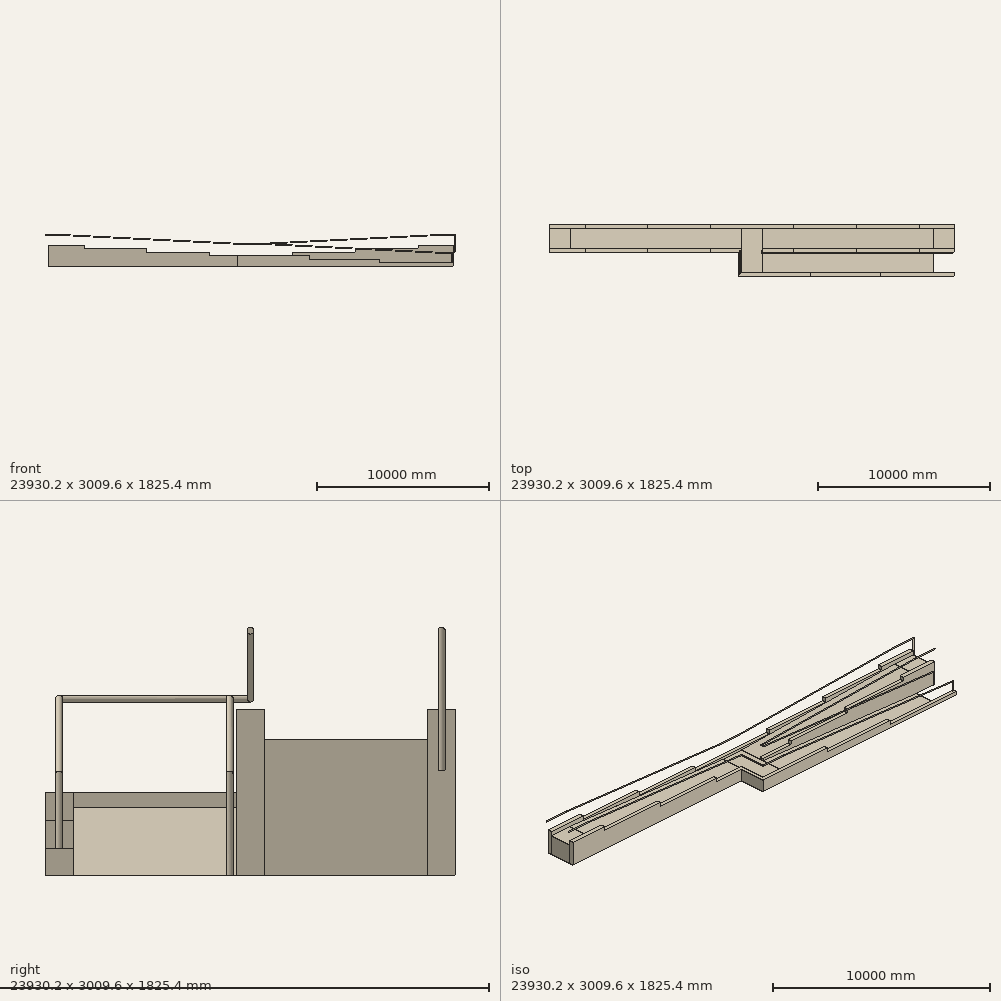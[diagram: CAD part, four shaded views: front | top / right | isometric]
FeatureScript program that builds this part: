
annotation { "Feature Type Name" : "Feature", "Feature Type Description" : "" }
export const myFeature = defineFeature(function(context is Context, id is Id, definition is map)
    precondition{}
    {
        {
            var Q0;
            Q0=qCreatedBy(makeId("Front.planeOp"),FACE);
            var sketch = newSketch(context, id + "F0", { "sketchPlane" : qUnion([Q0])});
            skLineSegment(sketch, "E0", {"start": v(0, 0) * mm, "end": v(-11200, 0) * mm});
            skLineSegment(sketch, "E1", {"start": v(-11200, 0) * mm, "end": v(-11200, 500) * mm});
            skLineSegment(sketch, "E2", {"start": v(-11200, 500) * mm, "end": v(-10000, 500) * mm});
            skLineSegment(sketch, "E3", {"start": v(-10000, 500) * mm, "end": v(0, 0) * mm});
            skLineSegment(sketch, "E4", {"start": v(0, 0) * mm, "end": v(1200, 0) * mm});
            skLineSegment(sketch, "E5", {"start": v(1200, 0) * mm, "end": v(1200, 1000) * mm});
            skLineSegment(sketch, "E6", {"start": v(1200, 1000) * mm, "end": v(0, 1000) * mm});
            skLineSegment(sketch, "E7", {"start": v(0, 1000) * mm, "end": v(-10000, 500) * mm});
            skLineSegment(sketch, "E8", {"start": v(0, 1000) * mm, "end": v(0, 0) * mm, "construction": true});
            skLineSegment(sketch, "E9", {"start": v(-10600, 500) * mm, "end": v(-10600, 2597.13) * mm, "construction": true});
            skLineSegment(sketch, "E10.MirrorCS", {"start": v(-21200, 1000) * mm, "end": v(-11200, 500) * mm});
            skLineSegment(sketch, "E11.MirrorCS", {"start": v(-22400, 1000) * mm, "end": v(-21200, 1000) * mm});
            skLineSegment(sketch, "E12.MirrorCS", {"start": v(-22400, 0) * mm, "end": v(-22400, 1000) * mm});
            skLineSegment(sketch, "E13.MirrorCS", {"start": v(-21200, 0) * mm, "end": v(-22400, 0) * mm});
            skLineSegment(sketch, "E14.MirrorCS", {"start": v(-21200, 0) * mm, "end": v(-10000, 0) * mm});
            skSolve(sketch);
        }
        {
            var Q0;
            Q0=makeQuery(id+"F0.imprint","IMPRINT",FACE,{"disambiguationData":[TD([[makeQuery(id+"F0.imprint","IMPRINT",EDGE,{"derivedFrom":sQuery(id+"F0.wireOp",EDGE,"E0")}),-1.0]])]});
            extrude(context, id + "F1", {"entities" : qUnion([Q0]), "depth" : 1200 * mm, "offsetDistance" : 25 * mm});
        }
        {
            var Q0;
            Q0=makeQuery(id+"F0.imprint","IMPRINT",FACE,{"disambiguationData":[TD([[makeQuery(id+"F0.imprint","IMPRINT",EDGE,{"derivedFrom":sQuery(id+"F0.wireOp",EDGE,"E3")}),1.0]])]});
            var Q1;
            Q1=makeQuery(id+"F0.imprint","IMPRINT",FACE,{"disambiguationData":[TD([[makeQuery(id+"F0.imprint","IMPRINT",EDGE,{"derivedFrom":sQuery(id+"F0.wireOp",EDGE,"E0")}),-1.0]])]});
            var Q2;
            {var subQ0=sQuery(id+"F0.wireOp",EDGE,"E1");Q2=makeQuery(id+"F0.imprint","IMPRINT",FACE,{"disambiguationData":[TD([[makeQuery(id+"F0.imprint","IMPRINT",EDGE,{"derivedFrom":subQ0}),1.0]])]});}
            extrude(context, id + "F2", {"entities" : qUnion([Q0, Q1, Q2]), "operationType" : NewBodyOperationType.ADD, "oppositeDirection" : true, "depth" : 203.2 * mm + 1200 * mm, "offsetDistance" : 25 * mm});
        }
        {
            var Q0;
            Q0=qCreatedBy(makeId("Top.planeOp"),FACE);
            var sketch = newSketch(context, id + "F3", { "sketchPlane" : qUnion([Q0])});
            skLineSegment(sketch, "E15.0", {"start": v(1200, 0) * mm, "end": v(0, 0) * mm, "construction": true});
            skLineSegment(sketch, "E15.1", {"start": v(-11200, 0) * mm, "end": v(-10000, 0) * mm, "construction": true});
            skLineSegment(sketch, "E16.bottom", {"start": v(-11200, 0) * mm, "end": v(1200, 0) * mm});
            skLineSegment(sketch, "E16.top", {"start": v(-10000, 203.2) * mm, "end": v(1200, 203.2) * mm});
            skLineSegment(sketch, "E16.left", {"start": v(-10000, 0) * mm, "end": v(-10000, 203.2) * mm});
            skLineSegment(sketch, "E16.right", {"start": v(1200, 0) * mm, "end": v(1200, 203.2) * mm});
            skLineSegment(sketch, "E17", {"start": v(-10600, 0) * mm, "end": v(-10600, 1718.88) * mm, "construction": true});
            skLineSegment(sketch, "E18.MirrorCS", {"start": v(-22400, 0) * mm, "end": v(-22400, 203.2) * mm});
            skLineSegment(sketch, "E19.MirrorCS", {"start": v(-11200, 0) * mm, "end": v(-11200, 203.2) * mm});
            skLineSegment(sketch, "E20.MirrorCS", {"start": v(-10000, 0) * mm, "end": v(-11200, 0) * mm, "construction": true});
            skLineSegment(sketch, "E21.MirrorCS", {"start": v(-22400, 0) * mm, "end": v(-21200, 0) * mm, "construction": true});
            skLineSegment(sketch, "E22.MirrorCS", {"start": v(-10000, 0) * mm, "end": v(-22400, 0) * mm});
            skLineSegment(sketch, "E23.MirrorCS", {"start": v(-11200, 203.2) * mm, "end": v(-22400, 203.2) * mm});
            skSolve(sketch);
        }
        {
            var Q0;
            Q0 = qSketchRegion(id + "F3", true);
            extrude(context, id + "F4", {"entities" : qUnion([Q0]), "operationType" : NewBodyOperationType.REMOVE, "endBound" : BoundingType.THROUGH_ALL, "depth" : 25 * mm, "offsetDistance" : 25 * mm});
        }
        {
            var Q0;
            Q0=sQuery(id+"F0.wireOp",EDGE,"E4");
            extrude(context, id + "F5", {"bodyType" : ToolBodyType.SURFACE, "surfaceEntities" : qUnion([Q0]), "depth" : 1200 * mm, "offsetDistance" : 25 * mm});
        }
        {
            var Q0;
            Q0=makeQuery(id+"F4.boolean.opBoolean","COPY",FACE,{"derivedFrom":makeQuery(id+"F4.opExtrude","SWEPT_FACE",FACE,{"disambiguationData":[OSD([sQuery(id+"F3.wireOp",EDGE,"E16.top")])]})});
            var sketch = newSketch(context, id + "F6", { "sketchPlane" : qUnion([Q0])});
            skLineSegment(sketch, "E24", {"start": v(-10000, 0) * mm, "end": v(-10000, 609.6) * mm});
            skLineSegment(sketch, "E25", {"start": v(-10000, 609.6) * mm, "end": v(-8171.2, 609.6) * mm});
            skLineSegment(sketch, "E26", {"start": v(-8171.2, 609.6) * mm, "end": v(-8171.2, 812.8) * mm});
            skLineSegment(sketch, "E27.1.0.1", {"start": v(-8171.2, 812.8) * mm, "end": v(-4513.6, 812.8) * mm});
            skLineSegment(sketch, "E28.1.0.0", {"start": v(-4513.6, 812.8) * mm, "end": v(-4513.6, 1016) * mm});
            skLineSegment(sketch, "E28.1.0.1", {"start": v(-4513.6, 1016) * mm, "end": v(-856, 1016) * mm});
            skLineSegment(sketch, "E28.2.0.0", {"start": v(-856, 1016) * mm, "end": v(-856, 1219.2) * mm});
            skLineSegment(sketch, "E28.direction1", {"start": v(-8171.2, 609.6) * mm, "end": v(-4513.6, 812.8) * mm, "construction": true});
            skLineSegment(sketch, "E29", {"start": v(-856, 1219.2) * mm, "end": v(1200, 1219.2) * mm});
            skLineSegment(sketch, "E30", {"start": v(1200, 1219.2) * mm, "end": v(1200, 0) * mm});
            skLineSegment(sketch, "E31", {"start": v(1200, 0) * mm, "end": v(-10000, 0) * mm});
            skLineSegment(sketch, "E32", {"start": v(-10600.94, 500.76) * mm, "end": v(-10600.94, 1723.23) * mm, "construction": true});
            skLineSegment(sketch, "E33.MirrorCS", {"start": v(-20345.88, 1016) * mm, "end": v(-20345.88, 1219.2) * mm});
            skLineSegment(sketch, "E34.MirrorCS", {"start": v(-13030.68, 609.6) * mm, "end": v(-13030.68, 812.8) * mm});
            skLineSegment(sketch, "E35.MirrorCS", {"start": v(-16688.28, 812.8) * mm, "end": v(-16688.28, 1016) * mm});
            skLineSegment(sketch, "E36.MirrorCS", {"start": v(-22401.88, 0) * mm, "end": v(-11201.88, 0) * mm});
            skLineSegment(sketch, "E37.MirrorCS", {"start": v(-20345.88, 1219.2) * mm, "end": v(-22401.88, 1219.2) * mm});
            skLineSegment(sketch, "E38.MirrorCS", {"start": v(-13030.68, 812.8) * mm, "end": v(-16688.28, 812.8) * mm});
            skLineSegment(sketch, "E39.MirrorCS", {"start": v(-11201.88, 0) * mm, "end": v(-11201.88, 609.6) * mm});
            skLineSegment(sketch, "E40.MirrorCS", {"start": v(-11201.88, 609.6) * mm, "end": v(-13030.68, 609.6) * mm});
            skLineSegment(sketch, "E41.MirrorCS", {"start": v(-13030.68, 609.6) * mm, "end": v(-16688.28, 812.8) * mm, "construction": true});
            skLineSegment(sketch, "E42.MirrorCS", {"start": v(-22401.88, 1219.2) * mm, "end": v(-22401.88, 0) * mm});
            skLineSegment(sketch, "E43.MirrorCS", {"start": v(-16688.28, 1016) * mm, "end": v(-20345.88, 1016) * mm});
            skSolve(sketch);
        }
        {
            var Q0;
            Q0 = qSketchRegion(id + "F6", true);
            extrude(context, id + "F7", {"entities" : qUnion([Q0]), "depth" : 203.2 * mm, "offsetDistance" : 25 * mm});
        }
        {
            var Q0;
            Q0=makeQuery(id+"F2.opExtrude","CAP_FACE",FACE,{"disambiguationData":[OSD([sQuery(id+"F0.wireOp",EDGE,"E0"),sQuery(id+"F0.wireOp",EDGE,"E1"),sQuery(id+"F0.wireOp",EDGE,"E2"),sQuery(id+"F0.wireOp",EDGE,"E4"),sQuery(id+"F0.wireOp",EDGE,"E5"),sQuery(id+"F0.wireOp",EDGE,"E6"),sQuery(id+"F0.wireOp",EDGE,"E7")])],"isStart":false});
            var sketch = newSketch(context, id + "F8", { "sketchPlane" : qUnion([Q0])});
            skLineSegment(sketch, "E44.0.0", {"start": v(10000, 0) * mm, "end": v(10000, 609.6) * mm, "construction": true});
            skLineSegment(sketch, "E44.0.1", {"start": v(10000, 609.6) * mm, "end": v(8171.2, 609.6) * mm});
            skLineSegment(sketch, "E44.0.2", {"start": v(8171.2, 609.6) * mm, "end": v(8171.2, 812.8) * mm});
            skLineSegment(sketch, "E44.0.3", {"start": v(8171.2, 812.8) * mm, "end": v(4513.6, 812.8) * mm});
            skLineSegment(sketch, "E44.0.4", {"start": v(4513.6, 812.8) * mm, "end": v(4513.6, 1016) * mm});
            skLineSegment(sketch, "E44.0.5", {"start": v(4513.6, 1016) * mm, "end": v(856, 1016) * mm});
            skLineSegment(sketch, "E44.0.6", {"start": v(856, 1016) * mm, "end": v(856, 1219.2) * mm});
            skLineSegment(sketch, "E44.0.7", {"start": v(856, 1219.2) * mm, "end": v(-1200, 1219.2) * mm});
            skLineSegment(sketch, "E44.0.8", {"start": v(-1200, 1219.2) * mm, "end": v(-1200, 0) * mm});
            skLineSegment(sketch, "E44.0.9", {"start": v(-1200, 0) * mm, "end": v(10000, 0) * mm});
            skLineSegment(sketch, "E45", {"start": v(11200, 609.6) * mm, "end": v(10000, 609.6) * mm});
            skLineSegment(sketch, "E46", {"start": v(10600, 609.6) * mm, "end": v(10600, -570.65) * mm, "construction": true});
            skLineSegment(sketch, "E47.MirrorCS", {"start": v(11200, 609.6) * mm, "end": v(13028.8, 609.6) * mm});
            skLineSegment(sketch, "E48.MirrorCS", {"start": v(13028.8, 609.6) * mm, "end": v(13028.8, 812.8) * mm});
            skLineSegment(sketch, "E49.MirrorCS", {"start": v(20344, 1016) * mm, "end": v(20344, 1219.2) * mm});
            skLineSegment(sketch, "E50.MirrorCS", {"start": v(16686.4, 812.8) * mm, "end": v(16686.4, 1016) * mm});
            skLineSegment(sketch, "E51.MirrorCS", {"start": v(16686.4, 1016) * mm, "end": v(20344, 1016) * mm});
            skLineSegment(sketch, "E52.MirrorCS", {"start": v(13028.8, 812.8) * mm, "end": v(16686.4, 812.8) * mm});
            skLineSegment(sketch, "E53.MirrorCS", {"start": v(22400, 1219.2) * mm, "end": v(22400, 0) * mm});
            skLineSegment(sketch, "E54.MirrorCS", {"start": v(20344, 1219.2) * mm, "end": v(22400, 1219.2) * mm});
            skLineSegment(sketch, "E55.MirrorCS", {"start": v(22400, 0) * mm, "end": v(11200, 0) * mm});
            skLineSegment(sketch, "E56", {"start": v(11200, 0) * mm, "end": v(10000, 0) * mm});
            skSolve(sketch);
        }
        {
            var Q0;
            Q0 = qSketchRegion(id + "F8", true);
            extrude(context, id + "F9", {"entities" : qUnion([Q0]), "depth" : 203.2 * mm, "offsetDistance" : 25 * mm});
        }
        {
            var Q0;
            Q0=makeQuery(id+"F1.opExtrude","SWEPT_FACE",FACE,{"disambiguationData":[OSD([sQuery(id+"F0.wireOp",EDGE,"E1")])]});
            var sketch = newSketch(context, id + "F10", { "sketchPlane" : qUnion([Q0])});
            skLineSegment(sketch, "E57.top", {"start": v(0, 0) * mm, "end": v(1200, 0) * mm});
            skLineSegment(sketch, "E57.right", {"start": v(1200, 609.6) * mm, "end": v(1200, 0) * mm, "construction": true});
            skLineSegment(sketch, "E58", {"start": v(1200, 609.6) * mm, "end": v(1403.2, 609.6) * mm});
            skLineSegment(sketch, "E59", {"start": v(1403.2, 609.6) * mm, "end": v(1403.2, 0) * mm});
            skLineSegment(sketch, "E60", {"start": v(1403.2, 0) * mm, "end": v(1200, 0) * mm});
            skLineSegment(sketch, "E61", {"start": v(1200, 609.6) * mm, "end": v(0, 609.6) * mm});
            skLineSegment(sketch, "E62", {"start": v(0, 609.6) * mm, "end": v(0, 0) * mm});
            skSolve(sketch);
        }
        {
            var Q0;
            Q0 = qSketchRegion(id + "F10", true);
            extrude(context, id + "F11", {"entities" : qUnion([Q0]), "operationType" : NewBodyOperationType.ADD, "depth" : 203.2 * mm, "offsetDistance" : 25 * mm});
        }
        {
            var Q0;
            Q0=makeQuery(id+"F1.opExtrude","CAP_FACE",FACE,{"disambiguationData":[OSD([sQuery(id+"F0.wireOp",EDGE,"E0"),sQuery(id+"F0.wireOp",EDGE,"E1"),sQuery(id+"F0.wireOp",EDGE,"E2"),sQuery(id+"F0.wireOp",EDGE,"E3")])],"isStart":false});
            var sketch = newSketch(context, id + "F12", { "sketchPlane" : qUnion([Q0])});
            skLineSegment(sketch, "E63", {"start": v(-11200, 500) * mm, "end": v(-11200, 609.6) * mm});
            skLineSegment(sketch, "E64", {"start": v(-11200, 609.6) * mm, "end": v(-7200, 609.6) * mm});
            skLineSegment(sketch, "E65", {"start": v(-7200, 609.6) * mm, "end": v(-7200, 406.4) * mm});
            skLineSegment(sketch, "E66", {"start": v(-7200, 406.4) * mm, "end": v(-3136, 406.4) * mm});
            skLineSegment(sketch, "E67.1.0.0", {"start": v(-3136, 406.4) * mm, "end": v(-3136, 203.2) * mm});
            skLineSegment(sketch, "E67.1.0.1", {"start": v(-3136, 203.2) * mm, "end": v(928, 203.2) * mm});
            skLineSegment(sketch, "E67.direction1", {"start": v(-7200, 406.4) * mm, "end": v(-3136, 203.2) * mm, "construction": true});
            skLineSegment(sketch, "E68.0", {"start": v(1200, 0) * mm, "end": v(1200, 1000) * mm, "construction": true});
            skLineSegment(sketch, "E69", {"start": v(928, 203.2) * mm, "end": v(1200, 203.2) * mm});
            skLineSegment(sketch, "E70", {"start": v(1200, 203.2) * mm, "end": v(1200, 0) * mm});
            skLineSegment(sketch, "E71", {"start": v(-11200, 500) * mm, "end": v(-11200, 0) * mm});
            skLineSegment(sketch, "E72", {"start": v(-11200, 0) * mm, "end": v(1200, 0) * mm});
            skSolve(sketch);
        }
        {
            var Q0;
            Q0 = qSketchRegion(id + "F12", true);
            extrude(context, id + "F13", {"entities" : qUnion([Q0]), "operationType" : NewBodyOperationType.ADD, "depth" : 203.2 * mm, "offsetDistance" : 25 * mm});
        }
        {
            var Q0;
            Q0=makeQuery(id+"F13.opExtrude","CAP_FACE",FACE,{"disambiguationData":[OSD([sQuery(id+"F12.wireOp",EDGE,"E63"),sQuery(id+"F12.wireOp",EDGE,"E64"),sQuery(id+"F12.wireOp",EDGE,"E65"),sQuery(id+"F12.wireOp",EDGE,"E66"),sQuery(id+"F12.wireOp",EDGE,"E67.1.0.0"),sQuery(id+"F12.wireOp",EDGE,"E67.1.0.1"),sQuery(id+"F12.wireOp",EDGE,"E69"),sQuery(id+"F12.wireOp",EDGE,"E70"),sQuery(id+"F12.wireOp",EDGE,"E71"),sQuery(id+"F12.wireOp",EDGE,"E72")])],"isStart":false});
            var Q1;
            Q1=makeQuery(id+"F13.opExtrude","CAP_FACE",FACE,{"disambiguationData":[OSD([sQuery(id+"F12.wireOp",EDGE,"E63"),sQuery(id+"F12.wireOp",EDGE,"E64"),sQuery(id+"F12.wireOp",EDGE,"E65"),sQuery(id+"F12.wireOp",EDGE,"E66"),sQuery(id+"F12.wireOp",EDGE,"E67.1.0.0"),sQuery(id+"F12.wireOp",EDGE,"E67.1.0.1"),sQuery(id+"F12.wireOp",EDGE,"E69"),sQuery(id+"F12.wireOp",EDGE,"E70"),sQuery(id+"F12.wireOp",EDGE,"E71"),sQuery(id+"F12.wireOp",EDGE,"E72")])],"isStart":true});
            cPlane(context, id + "F14", {"entities" : qUnion([Q0, Q1]), "cplaneType" : CPlaneType.MID_PLANE, "offset" : 25 * mm, "width" : 150 * mm, "height" : 150 * mm});
        }
        {
            var Q0;
            Q0=qCreatedBy(id+"F14.planeOp",FACE);
            var sketch = newSketch(context, id + "F15", { "sketchPlane" : qUnion([Q0])});
            skLineSegment(sketch, "E73", {"start": v(1098.4, 0) * mm, "end": v(1098.4, 745.08) * mm});
            skLineSegment(sketch, "E74", {"start": v(1098.4, 745.08) * mm, "end": v(-10000, 1300) * mm});
            skLineSegment(sketch, "E75", {"start": v(-10000, 1300) * mm, "end": v(-10000, 609.6) * mm, "construction": true});
            skLineSegment(sketch, "E76", {"start": v(0, 0) * mm, "end": v(0, 800) * mm, "construction": true});
            skSolve(sketch);
        }
        {
            var Q0;
            {var subQ0=sQuery(id+"F0.wireOp",EDGE,"E2");Q0=makeQuery(id+"F2.boolean.opBoolean","MERGE",FACE,{"derivedFrom":[makeQuery(id+"F1.opExtrude","SWEPT_FACE",FACE,{"disambiguationData":[OSD([subQ0])]}),makeQuery(id+"F2.opExtrude","SWEPT_FACE",FACE,{"disambiguationData":[OSD([subQ0])]})]});}
            var Q1;
            Q1=sQuery(id+"F15.wireOp",VERTEX,"E75.start");
            cPlane(context, id + "F16", {"entities" : qUnion([Q0, Q1]), "cplaneType" : CPlaneType.PLANE_POINT, "offset" : 25 * mm, "width" : 150 * mm, "height" : 150 * mm});
        }
        {
            var Q0;
            Q0=makeQuery(id+"F9.opExtrude","CAP_FACE",FACE,{"disambiguationData":[OSD([sQuery(id+"F8.wireOp",EDGE,"E44.0.1"),sQuery(id+"F8.wireOp",EDGE,"E44.0.2"),sQuery(id+"F8.wireOp",EDGE,"E44.0.3"),sQuery(id+"F8.wireOp",EDGE,"E44.0.4"),sQuery(id+"F8.wireOp",EDGE,"E44.0.5"),sQuery(id+"F8.wireOp",EDGE,"E44.0.6"),sQuery(id+"F8.wireOp",EDGE,"E44.0.7"),sQuery(id+"F8.wireOp",EDGE,"E44.0.8"),sQuery(id+"F8.wireOp",EDGE,"E44.0.9"),sQuery(id+"F8.wireOp",EDGE,"E45"),sQuery(id+"F8.wireOp",EDGE,"E48.MirrorCS"),sQuery(id+"F8.wireOp",EDGE,"E49.MirrorCS"),sQuery(id+"F8.wireOp",EDGE,"E50.MirrorCS"),sQuery(id+"F8.wireOp",EDGE,"E51.MirrorCS"),sQuery(id+"F8.wireOp",EDGE,"E52.MirrorCS"),sQuery(id+"F8.wireOp",EDGE,"E53.MirrorCS"),sQuery(id+"F8.wireOp",EDGE,"E47.MirrorCS"),sQuery(id+"F8.wireOp",EDGE,"E54.MirrorCS"),sQuery(id+"F8.wireOp",EDGE,"E55.MirrorCS"),sQuery(id+"F8.wireOp",EDGE,"E56")])],"isStart":true});
            var Q1;
            Q1=makeQuery(id+"F9.opExtrude","CAP_FACE",FACE,{"disambiguationData":[OSD([sQuery(id+"F8.wireOp",EDGE,"E44.0.1"),sQuery(id+"F8.wireOp",EDGE,"E44.0.2"),sQuery(id+"F8.wireOp",EDGE,"E44.0.3"),sQuery(id+"F8.wireOp",EDGE,"E44.0.4"),sQuery(id+"F8.wireOp",EDGE,"E44.0.5"),sQuery(id+"F8.wireOp",EDGE,"E44.0.6"),sQuery(id+"F8.wireOp",EDGE,"E44.0.7"),sQuery(id+"F8.wireOp",EDGE,"E44.0.8"),sQuery(id+"F8.wireOp",EDGE,"E44.0.9"),sQuery(id+"F8.wireOp",EDGE,"E45"),sQuery(id+"F8.wireOp",EDGE,"E48.MirrorCS"),sQuery(id+"F8.wireOp",EDGE,"E49.MirrorCS"),sQuery(id+"F8.wireOp",EDGE,"E50.MirrorCS"),sQuery(id+"F8.wireOp",EDGE,"E51.MirrorCS"),sQuery(id+"F8.wireOp",EDGE,"E52.MirrorCS"),sQuery(id+"F8.wireOp",EDGE,"E53.MirrorCS"),sQuery(id+"F8.wireOp",EDGE,"E47.MirrorCS"),sQuery(id+"F8.wireOp",EDGE,"E54.MirrorCS"),sQuery(id+"F8.wireOp",EDGE,"E55.MirrorCS"),sQuery(id+"F8.wireOp",EDGE,"E56")])],"isStart":false});
            cPlane(context, id + "F17", {"entities" : qUnion([Q0, Q1]), "cplaneType" : CPlaneType.MID_PLANE, "offset" : 25 * mm, "width" : 150 * mm, "height" : 150 * mm});
        }
        {
            var Q0;
            Q0=qCreatedBy(id+"F16.planeOp",FACE);
            var sketch = newSketch(context, id + "F18", { "sketchPlane" : qUnion([Q0])});
            skLineSegment(sketch, "E77", {"start": v(-10000, -1301.6) * mm, "end": v(-11301.6, -1301.6) * mm});
            skLineSegment(sketch, "E78.0", {"start": v(-11200, 1403.2) * mm, "end": v(-11200, -1200) * mm, "construction": true});
            skLineSegment(sketch, "E78.1", {"start": v(-11403.2, 1606.4) * mm, "end": v(-11403.2, -1403.2) * mm, "construction": true});
            skLineSegment(sketch, "E79", {"start": v(-11200, -1200) * mm, "end": v(-11403.2, -1403.2) * mm, "construction": true});
            skLineSegment(sketch, "E80", {"start": v(-11403.2, 1606.4) * mm, "end": v(-11200, 1403.2) * mm, "construction": true});
            skLineSegment(sketch, "E81", {"start": v(-11301.6, -1301.6) * mm, "end": v(-11301.6, 101.6) * mm});
            skLineSegment(sketch, "E82", {"start": v(-11301.6, 1504.8) * mm, "end": v(-10000, 1504.8) * mm});
            skLineSegment(sketch, "E83", {"start": v(-10000, -1301.6) * mm, "end": v(-10000, 1504.8) * mm, "construction": true});
            skLineSegment(sketch, "E84.0", {"start": v(-10000, 0) * mm, "end": v(-10000, 203.2) * mm, "construction": true});
            skLineSegment(sketch, "E85", {"start": v(-10000, 101.6) * mm, "end": v(-10000, -50.8) * mm});
            skPoint(sketch, "E86", {"position": v(-11301.6, 101.6) * mm});
            skSolve(sketch);
        }
        {
            var Q0;
            Q0=qCreatedBy(id+"F17.planeOp",FACE);
            var sketch = newSketch(context, id + "F19", { "sketchPlane" : qUnion([Q0])});
            skLineSegment(sketch, "E87", {"start": v(0, 1800) * mm, "end": v(-10000, 1300) * mm});
            skLineSegment(sketch, "E88", {"start": v(1301.6, 1800) * mm, "end": v(0, 1800) * mm});
            skLineSegment(sketch, "E89", {"start": v(1301.6, 1800) * mm, "end": v(1301.6, 773.02) * mm});
            skPoint(sketch, "E90", {"position": v(-10650.8, 1300) * mm});
            skLineSegment(sketch, "E91", {"start": v(-10650.8, 1300) * mm, "end": v(-10650.8, 959.1) * mm, "construction": true});
            skLineSegment(sketch, "E92.MirrorCS", {"start": v(-21301.6, 1800) * mm, "end": v(-11301.6, 1300) * mm});
            skLineSegment(sketch, "E93.MirrorCS", {"start": v(-22603.2, 1800) * mm, "end": v(-21301.6, 1800) * mm});
            skLineSegment(sketch, "E94.MirrorCS", {"start": v(-22603.2, 1800) * mm, "end": v(-22603.2, 773.02) * mm});
            skSolve(sketch);
        }
        {
            var Q0;
            Q0=makeQuery(id+"F7.opExtrude","CAP_FACE",FACE,{"disambiguationData":[OSD([sQuery(id+"F6.wireOp",EDGE,"E24"),sQuery(id+"F6.wireOp",EDGE,"E25"),sQuery(id+"F6.wireOp",EDGE,"E26"),sQuery(id+"F6.wireOp",EDGE,"E27.1.0.1"),sQuery(id+"F6.wireOp",EDGE,"E28.1.0.0"),sQuery(id+"F6.wireOp",EDGE,"E28.1.0.1"),sQuery(id+"F6.wireOp",EDGE,"E28.2.0.0"),sQuery(id+"F6.wireOp",EDGE,"E29"),sQuery(id+"F6.wireOp",EDGE,"E30"),sQuery(id+"F6.wireOp",EDGE,"E31")])],"isStart":false});
            var Q1;
            Q1=makeQuery(id+"F7.opExtrude","CAP_FACE",FACE,{"disambiguationData":[OSD([sQuery(id+"F6.wireOp",EDGE,"E24"),sQuery(id+"F6.wireOp",EDGE,"E25"),sQuery(id+"F6.wireOp",EDGE,"E26"),sQuery(id+"F6.wireOp",EDGE,"E27.1.0.1"),sQuery(id+"F6.wireOp",EDGE,"E28.1.0.0"),sQuery(id+"F6.wireOp",EDGE,"E28.1.0.1"),sQuery(id+"F6.wireOp",EDGE,"E28.2.0.0"),sQuery(id+"F6.wireOp",EDGE,"E29"),sQuery(id+"F6.wireOp",EDGE,"E30"),sQuery(id+"F6.wireOp",EDGE,"E31")])],"isStart":true});
            cPlane(context, id + "F20", {"entities" : qUnion([Q0, Q1]), "cplaneType" : CPlaneType.MID_PLANE, "offset" : 25 * mm, "width" : 150 * mm, "height" : 150 * mm});
        }
        {
            var Q0;
            Q0=qCreatedBy(id+"F20.planeOp",FACE);
            var sketch = newSketch(context, id + "F21", { "sketchPlane" : qUnion([Q0])});
            skLineSegment(sketch, "E95.0", {"start": v(1301.6, 1800) * mm, "end": v(1301.6, 773.02) * mm});
            skLineSegment(sketch, "E95.1", {"start": v(1301.6, 1800) * mm, "end": v(0, 1800) * mm});
            skLineSegment(sketch, "E95.2", {"start": v(0, 1800) * mm, "end": v(-10000, 1300) * mm});
            skLineSegment(sketch, "E96.MirrorCS", {"start": v(-21301.6, 1800) * mm, "end": v(-11301.6, 1300) * mm});
            skLineSegment(sketch, "E97.MirrorCS", {"start": v(-22603.2, 1800) * mm, "end": v(-21301.6, 1800) * mm});
            skLineSegment(sketch, "E98.MirrorCS", {"start": v(-22603.2, 1800) * mm, "end": v(-22603.2, 773.02) * mm});
            skSolve(sketch);
        }
        {
            var Q0;
            Q0=sQuery(id+"F18.wireOp",VERTEX,"E85.end");
            var Q1;
            Q1=makeQuery(id+"F7.opExtrude","CAP_FACE",FACE,{"disambiguationData":[OSD([sQuery(id+"F6.wireOp",EDGE,"E24"),sQuery(id+"F6.wireOp",EDGE,"E25"),sQuery(id+"F6.wireOp",EDGE,"E26"),sQuery(id+"F6.wireOp",EDGE,"E27.1.0.1"),sQuery(id+"F6.wireOp",EDGE,"E28.1.0.0"),sQuery(id+"F6.wireOp",EDGE,"E28.1.0.1"),sQuery(id+"F6.wireOp",EDGE,"E28.2.0.0"),sQuery(id+"F6.wireOp",EDGE,"E29"),sQuery(id+"F6.wireOp",EDGE,"E30"),sQuery(id+"F6.wireOp",EDGE,"E31")])],"isStart":false});
            cPlane(context, id + "F22", {"entities" : qUnion([Q0, Q1]), "cplaneType" : CPlaneType.PLANE_POINT, "offset" : 25 * mm, "width" : 150 * mm, "height" : 150 * mm});
        }
        {
            var Q0;
            Q0=qCreatedBy(id+"F22.planeOp",FACE);
            var sketch = newSketch(context, id + "F23", { "sketchPlane" : qUnion([Q0])});
            skLineSegment(sketch, "E99.0", {"start": v(1098.4, 0) * mm, "end": v(1098.4, 745.08) * mm});
            skLineSegment(sketch, "E99.1", {"start": v(1098.4, 745.08) * mm, "end": v(-10000, 1300) * mm});
            skSolve(sketch);
        }
        {
            var Q0;
            Q0=qCreatedBy(makeId("Top.planeOp"),FACE);
            var sketch = newSketch(context, id + "F24", { "sketchPlane" : qUnion([Q0])});
            skCircle(sketch, "E100", {"center": v(1098.4, -1301.6) * mm, "radius": 25.4 * mm});
            skCircle(sketch, "E101", {"center": v(1098.4, -50.8) * mm, "radius": 25.4 * mm, "construction": true});
            skSolve(sketch);
        }
        {
            var Q0;
            Q0 = qSketchRegion(id + "F24", true);
            var Q1;
            Q1=sQuery(id+"F15.wireOp",EDGE,"E73");
            var Q2;
            Q2=sQuery(id+"F15.wireOp",EDGE,"E74");
            var Q3;
            Q3=sQuery(id+"F21.wireOp",EDGE,"E97.MirrorCS");
            var Q4;
            Q4=sQuery(id+"F18.wireOp",EDGE,"E77");
            var Q5;
            Q5=sQuery(id+"F18.wireOp",EDGE,"E81");
            var Q6;
            Q6=sQuery(id+"F21.wireOp",EDGE,"E96.MirrorCS");
            sweep(context, id + "F25", {"profiles" : qUnion([Q0]), "path" : qUnion([Q1, Q2, Q3, Q4, Q5, Q6])});
        }
        {
            var Q0;
            Q0=qCreatedBy(makeId("Top.planeOp"),FACE);
            var sketch = newSketch(context, id + "F26", { "sketchPlane" : qUnion([Q0])});
            skCircle(sketch, "E102.0", {"center": v(1098.4, -50.8) * mm, "radius": 25.4 * mm});
            skSolve(sketch);
        }
        {
            var Q0;
            Q0=makeQuery(id+"F26.imprint","IMPRINT",FACE,{"disambiguationData":[TD([[makeQuery(id+"F26.imprint","IMPRINT",EDGE,{"derivedFrom":sQuery(id+"F26.wireOp",EDGE,"E102.0")}),1.0]])]});
            var Q1;
            Q1=sQuery(id+"F26.wireOp",EDGE,"E102.0");
            var Q2;
            Q2=sQuery(id+"F23.wireOp",EDGE,"E99.0");
            var Q3;
            Q3=sQuery(id+"F21.wireOp",EDGE,"E95.1");
            var Q4;
            Q4=sQuery(id+"F23.wireOp",EDGE,"E99.1");
            var Q5;
            Q5=sQuery(id+"F21.wireOp",EDGE,"E95.2");
            var Q6;
            Q6=sQuery(id+"F18.wireOp",EDGE,"E85");
            sweep(context, id + "F27", {"profiles" : qUnion([Q0]), "surfaceProfiles" : qUnion([Q1]), "path" : qUnion([Q2, Q3, Q4, Q5, Q6])});
        }
        {
            var Q0;
            Q0=sQuery(id+"F19.wireOp",VERTEX,"E89.end");
            var Q1;
            Q1=qCreatedBy(makeId("Top.planeOp"),FACE);
            cPlane(context, id + "F28", {"entities" : qUnion([Q0, Q1]), "cplaneType" : CPlaneType.PLANE_POINT, "offset" : 25 * mm, "width" : 150 * mm, "height" : 150 * mm});
        }
        {
            var Q0;
            Q0=qCreatedBy(id+"F28.planeOp",FACE);
            var sketch = newSketch(context, id + "F29", { "sketchPlane" : qUnion([Q0])});
            skCircle(sketch, "E103", {"center": v(1301.6, 1504.8) * mm, "radius": 25.4 * mm});
            skSolve(sketch);
        }
        {
            var Q0;
            Q0 = qSketchRegion(id + "F29", true);
            var Q1;
            Q1=sQuery(id+"F19.wireOp",EDGE,"E88");
            var Q2;
            Q2=sQuery(id+"F19.wireOp",EDGE,"E87");
            var Q3;
            Q3=sQuery(id+"F18.wireOp",EDGE,"E82");
            var Q4;
            Q4=sQuery(id+"F19.wireOp",EDGE,"E92.MirrorCS");
            var Q5;
            Q5=sQuery(id+"F19.wireOp",EDGE,"E93.MirrorCS");
            var Q6;
            Q6=sQuery(id+"F19.wireOp",EDGE,"E89");
            sweep(context, id + "F30", {"profiles" : qUnion([Q0]), "path" : qUnion([Q1, Q2, Q3, Q4, Q5, Q6])});
        }
    });
